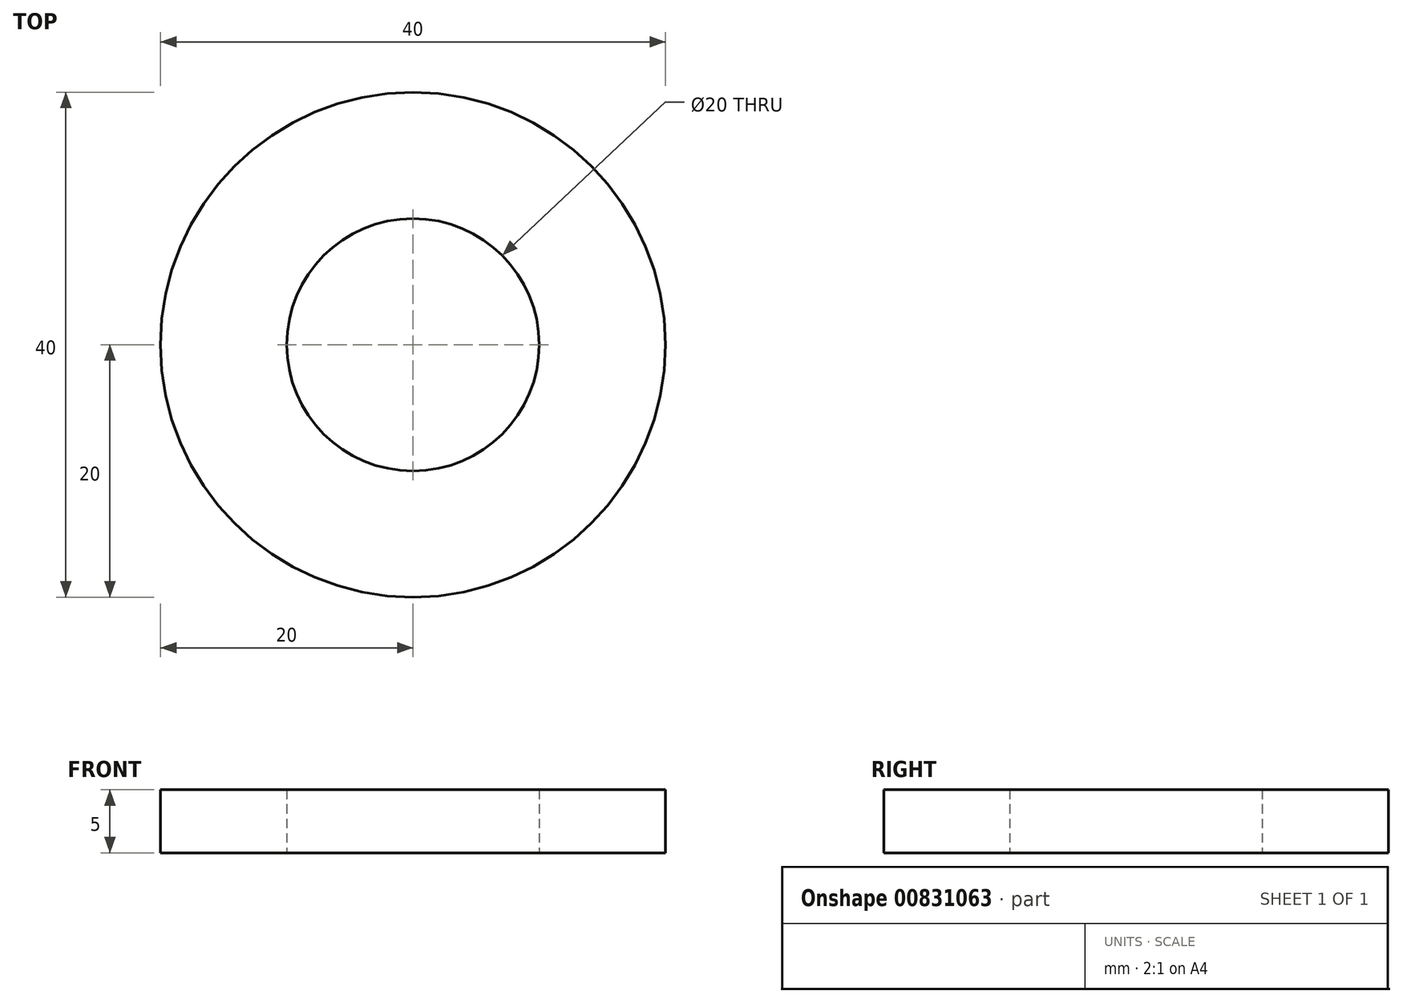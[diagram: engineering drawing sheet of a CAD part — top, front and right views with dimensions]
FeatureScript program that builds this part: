
annotation { "Feature Type Name" : "Feature", "Feature Type Description" : "" }
export const myFeature = defineFeature(function(context is Context, id is Id, definition is map)
    precondition{}
    {
        {
            var Q0;
            Q0=qCreatedBy(makeId("Top.planeOp"),FACE);
            var sketch = newSketch(context, id + "F0", { "sketchPlane" : qUnion([Q0])});
            skCircle(sketch, "E0", {"center": v(0, 0) * mm, "radius": 20 * mm});
            skCircle(sketch, "E1", {"center": v(0, 0) * mm, "radius": 10 * mm});
            skSolve(sketch);
        }
        {
            var Q0;
            Q0=makeQuery(id+"F0.imprint","IMPRINT",FACE,{"disambiguationData":[TD([[makeQuery(id+"F0.imprint","IMPRINT",EDGE,{"derivedFrom":sQuery(id+"F0.wireOp",EDGE,"E0")}),1.0]])]});
            extrude(context, id + "F1", {"entities" : qUnion([Q0]), "depth" : 5 * mm, "offsetDistance" : 25 * mm});
        }
    });
